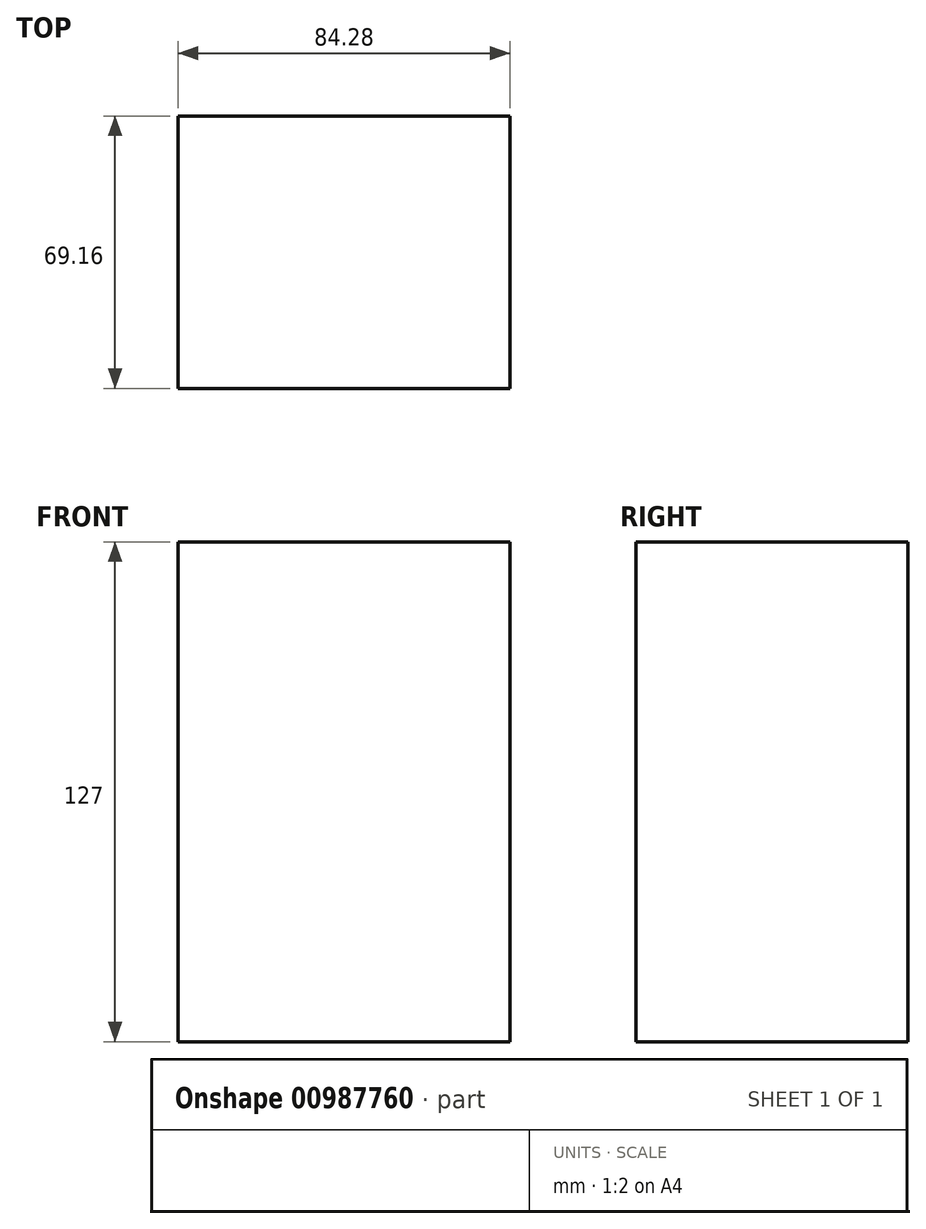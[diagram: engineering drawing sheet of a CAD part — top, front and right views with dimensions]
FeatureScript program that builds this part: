
annotation { "Feature Type Name" : "Feature", "Feature Type Description" : "" }
export const myFeature = defineFeature(function(context is Context, id is Id, definition is map)
    precondition{}
    {
        {
            var Q0;
            Q0=qCreatedBy(makeId("Top.planeOp"),FACE);
            var sketch = newSketch(context, id + "F0", { "sketchPlane" : qUnion([Q0])});
            skLineSegment(sketch, "E0.bottom", {"start": v(-42.38, 28.7) * mm, "end": v(41.9, 28.7) * mm});
            skLineSegment(sketch, "E0.top", {"start": v(-42.38, -40.46) * mm, "end": v(41.9, -40.46) * mm});
            skLineSegment(sketch, "E0.left", {"start": v(-42.38, 28.7) * mm, "end": v(-42.38, -40.46) * mm});
            skLineSegment(sketch, "E0.right", {"start": v(41.9, 28.7) * mm, "end": v(41.9, -40.46) * mm});
            skSolve(sketch);
        }
        {
            var Q0;
            Q0=makeQuery(id+"F0.imprint","IMPRINT",FACE,{"disambiguationData":[TD([[makeQuery(id+"F0.imprint","IMPRINT",EDGE,{"derivedFrom":sQuery(id+"F0.wireOp",EDGE,"E0.bottom")}),-1.0]])]});
            extrude(context, id + "F1", {"entities" : qUnion([Q0]), "depth" : 127 * mm, "offsetDistance" : 25.4 * mm});
        }
    });
